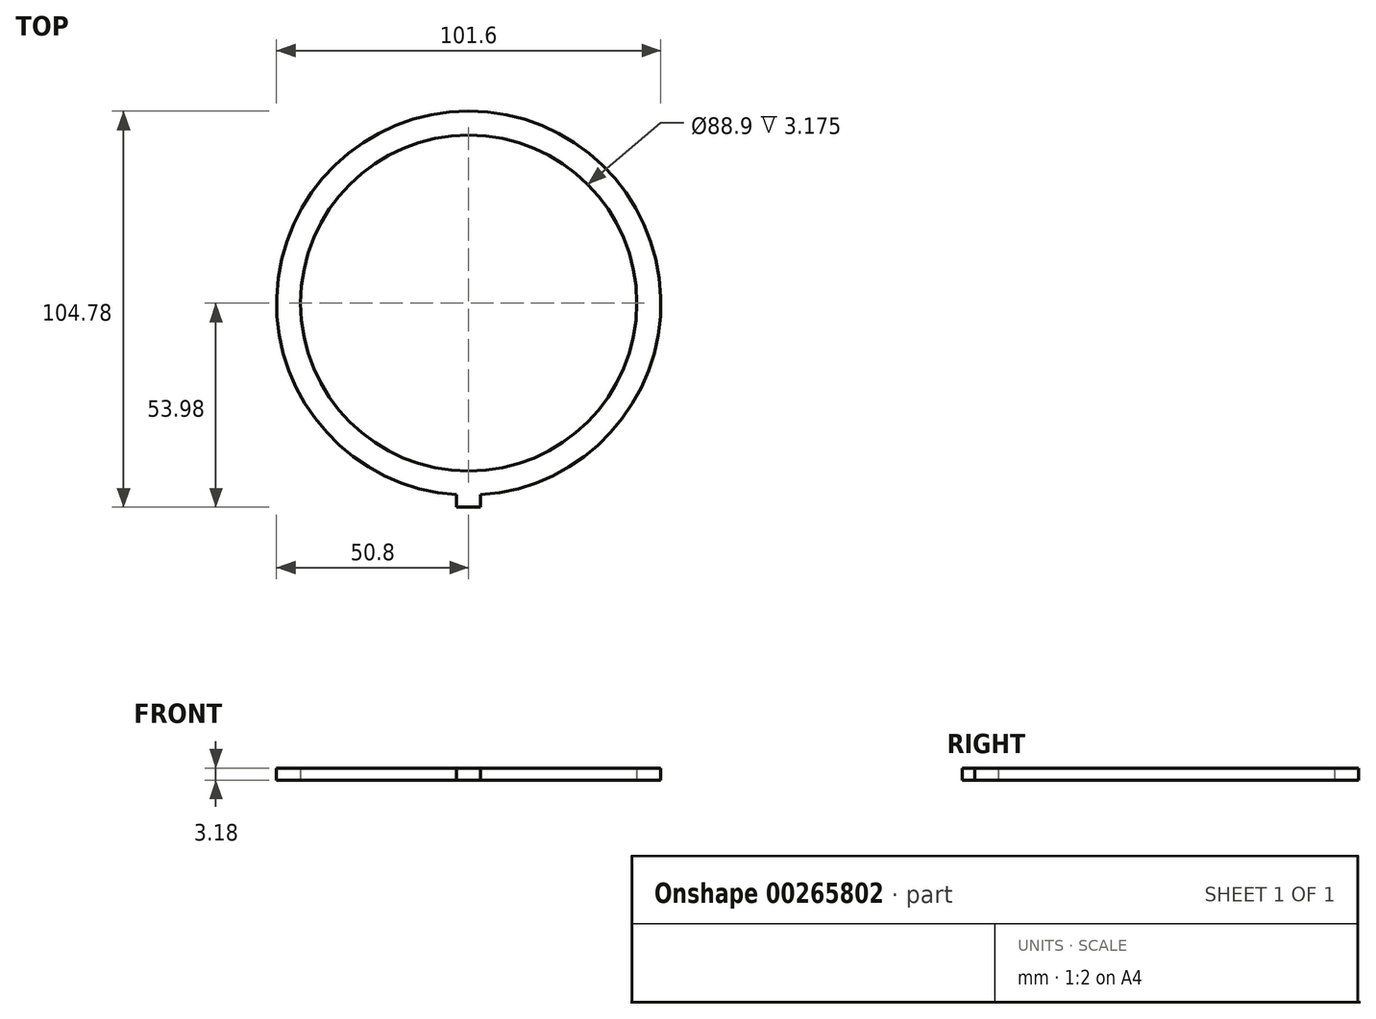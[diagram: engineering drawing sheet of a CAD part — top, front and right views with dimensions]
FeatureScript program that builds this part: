
annotation { "Feature Type Name" : "Feature", "Feature Type Description" : "" }
export const myFeature = defineFeature(function(context is Context, id is Id, definition is map)
    precondition{}
    {
        {
            var Q0;
            Q0=qCreatedBy(makeId("Top.planeOp"),FACE);
            var sketch = newSketch(context, id + "F0", { "sketchPlane" : qUnion([Q0])});
            skCircle(sketch, "E0", {"center": v(0, 0) * mm, "radius": 44.45 * mm});
            skCircle(sketch, "E1", {"center": v(0, 0) * mm, "radius": 50.8 * mm});
            skPoint(sketch, "E2", {"position": v(50.8, 0) * mm});
            skPoint(sketch, "E3", {"position": v(-50.8, 0) * mm});
            skPoint(sketch, "E4", {"position": v(0, 50.8) * mm});
            skPoint(sketch, "E5", {"position": v(0, -50.8) * mm});
            skLineSegment(sketch, "E6.bottom", {"start": v(-3.18, -53.98) * mm, "end": v(3.18, -53.98) * mm});
            skLineSegment(sketch, "E6.top", {"start": v(-3.18, -47.62) * mm, "end": v(3.17, -47.62) * mm});
            skLineSegment(sketch, "E6.left", {"start": v(-3.18, -53.98) * mm, "end": v(-3.18, -47.63) * mm});
            skLineSegment(sketch, "E6.right", {"start": v(3.18, -53.98) * mm, "end": v(3.17, -47.63) * mm});
            skSolve(sketch);
        }
        {
            var Q0;
            Q0 = qSketchRegion(id + "F0", true);
            extrude(context, id + "F1", {"entities" : qUnion([Q0]), "depth" : 3.17 * mm});
        }
    });
